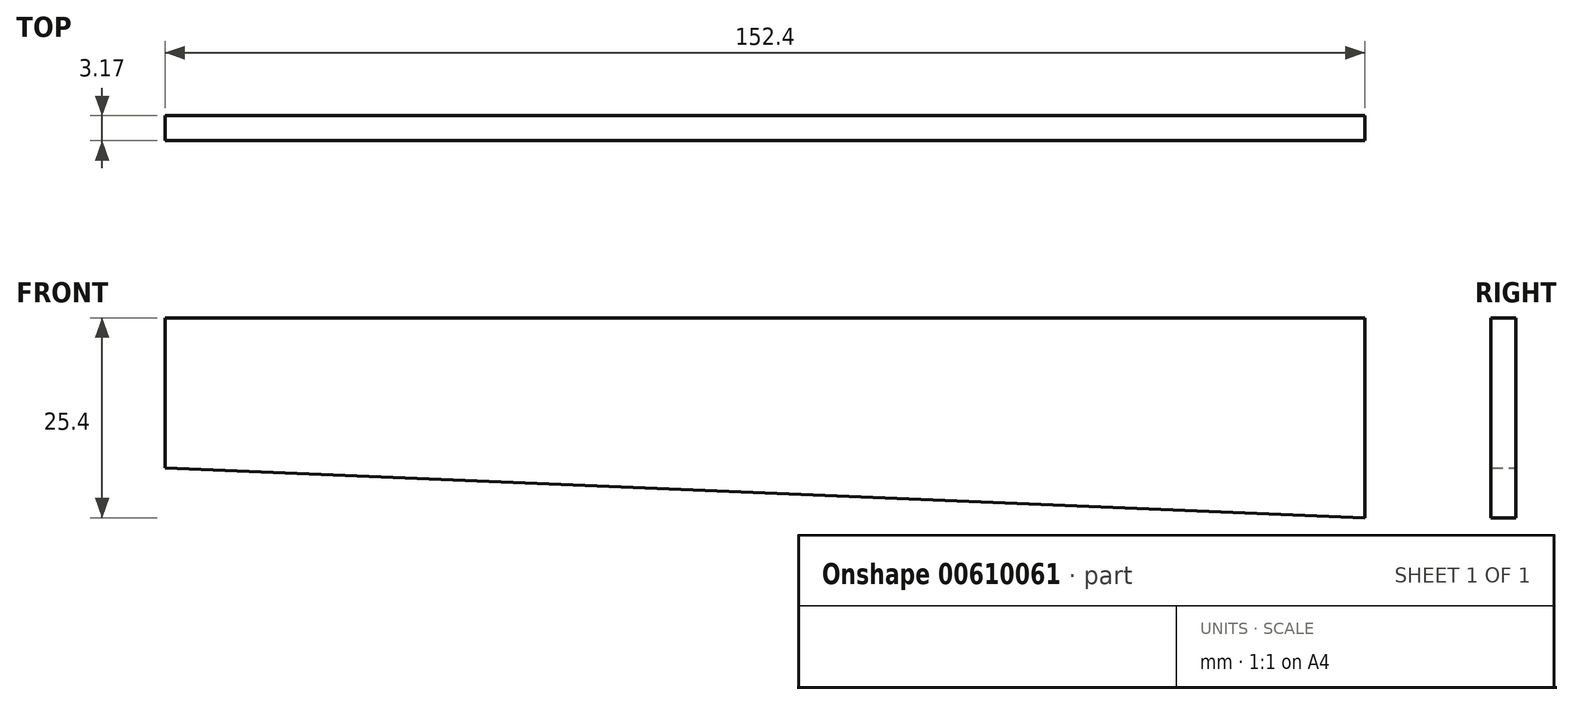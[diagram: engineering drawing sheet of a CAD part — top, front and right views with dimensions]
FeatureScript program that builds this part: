
annotation { "Feature Type Name" : "Feature", "Feature Type Description" : "" }
export const myFeature = defineFeature(function(context is Context, id is Id, definition is map)
    precondition{}
    {
        {
            var Q0;
            Q0=qCreatedBy(makeId("Front.planeOp"),FACE);
            var sketch = newSketch(context, id + "F0", { "sketchPlane" : qUnion([Q0])});
            skLineSegment(sketch, "E0", {"start": v(0, 0) * mm, "end": v(152.4, 0) * mm});
            skLineSegment(sketch, "E1", {"start": v(152.4, 0) * mm, "end": v(152.4, -25.4) * mm});
            skLineSegment(sketch, "E2", {"start": v(152.4, -25.4) * mm, "end": v(0, -19.05) * mm});
            skLineSegment(sketch, "E3", {"start": v(0, -19.05) * mm, "end": v(0, 0) * mm});
            skSolve(sketch);
        }
        {
            var Q0;
            Q0=makeQuery(id+"F0.imprint","IMPRINT",FACE,{"disambiguationData":[TD([[makeQuery(id+"F0.imprint","IMPRINT",EDGE,{"derivedFrom":sQuery(id+"F0.wireOp",EDGE,"E0")}),-1.0]])]});
            extrude(context, id + "F1", {"entities" : qUnion([Q0]), "depth" : 3.17 * mm, "offsetDistance" : 25.4 * mm});
        }
    });
